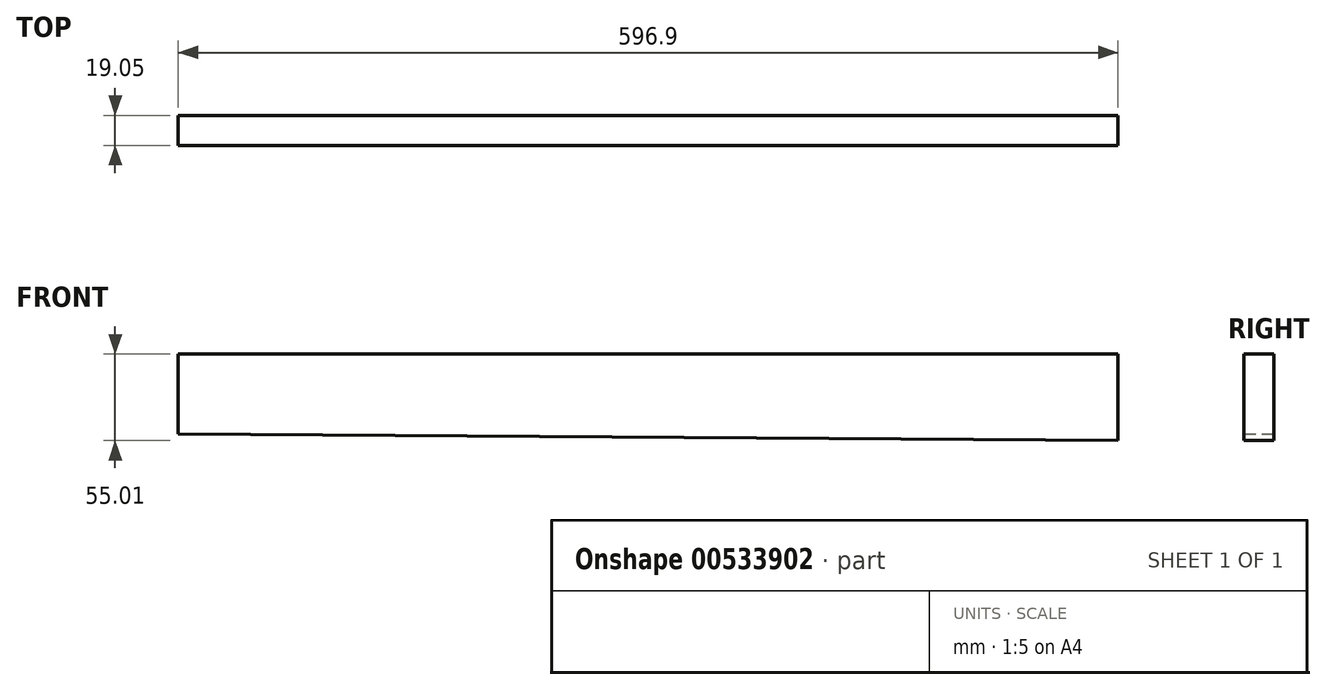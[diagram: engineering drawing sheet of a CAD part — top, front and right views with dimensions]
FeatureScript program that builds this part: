
annotation { "Feature Type Name" : "Feature", "Feature Type Description" : "" }
export const myFeature = defineFeature(function(context is Context, id is Id, definition is map)
    precondition{}
    {
        {
            var Q0;
            Q0=qCreatedBy(makeId("Front.planeOp"),FACE);
            var sketch = newSketch(context, id + "F0", { "sketchPlane" : qUnion([Q0])});
            skLineSegment(sketch, "E0", {"start": v(194.61, 55.01) * mm, "end": v(194.61, 4.21) * mm});
            skLineSegment(sketch, "E1", {"start": v(194.61, 4.21) * mm, "end": v(791.51, 0) * mm});
            skLineSegment(sketch, "E2", {"start": v(791.51, 0) * mm, "end": v(791.51, 55.01) * mm});
            skLineSegment(sketch, "E3", {"start": v(194.61, 55.01) * mm, "end": v(791.51, 55.01) * mm});
            skSolve(sketch);
        }
        {
            var Q0;
            Q0 = qSketchRegion(id + "F0", true);
            extrude(context, id + "F1", {"entities" : qUnion([Q0]), "depth" : 19.05 * mm, "offsetDistance" : 25.4 * mm});
        }
    });
